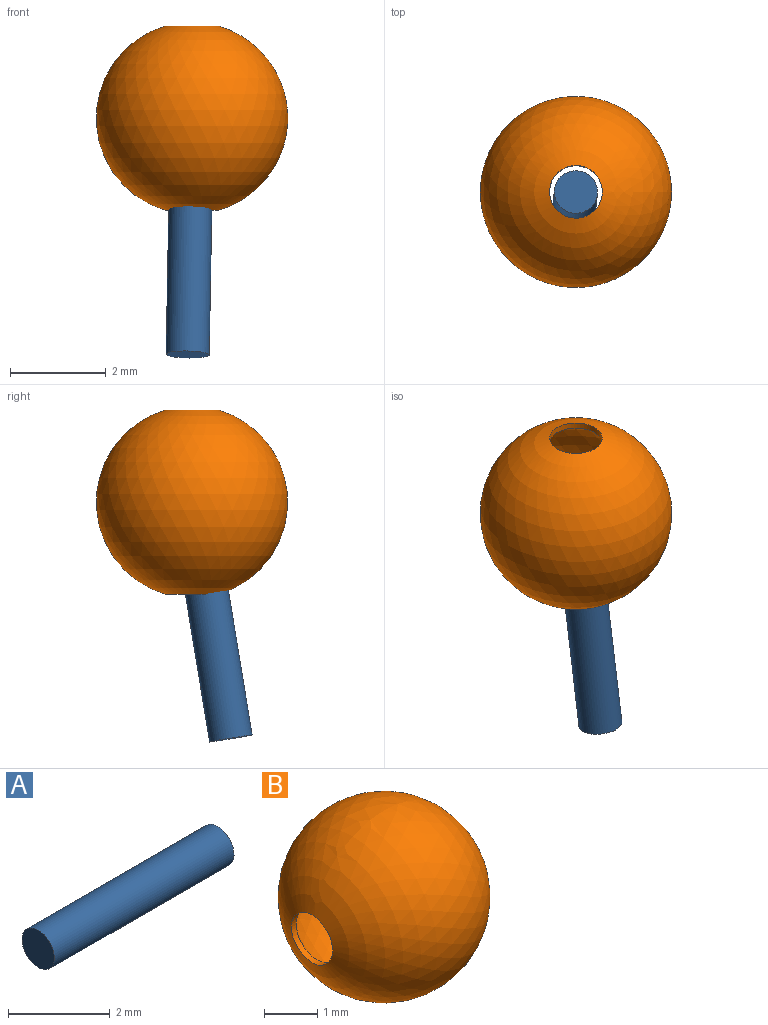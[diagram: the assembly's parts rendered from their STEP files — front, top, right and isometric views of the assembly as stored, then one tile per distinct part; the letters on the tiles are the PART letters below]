
ASSEMBLY  parts=2 mates=1
PART A: 3 faces, bbox 5x0.9x0.9 mm
  f0: plane 0.9x0.9mm, normal (1,0,0), area 0.6mm2, adj f2
  f1: plane 0.9x0.9mm, normal (-1,0,0), area 0.6mm2, adj f2
  f2: cylinder r=0.45mm len=5mm, axis (-1,0,0), area 14.1mm2, adj f0,f1
PART B: 4 faces, bbox 3.8x4x4 mm
  f0: sphere r=2mm, area 48.3mm2, adj f1,f3
  f1: cylinder r=0.55mm len=1.1mm, axis (-1,0,0), area 0.5mm2, adj f0,f2
  f2: sphere r=1.88mm, area 42.2mm2, adj f1,f3
  f3: cylinder r=0.55mm len=1.1mm, axis (-1,0,0), area 0.5mm2, adj f0,f2
PLACE A rot(axis=(-0.03,0.99,-0.14),91.1deg) t=(0,0,0)mm
PLACE B rot(axis=(0,1,0),90deg) t=(0,0,0)mm
MATE ball B.f1 <-> A.f2  axis (0,0,1) through (0,0,0)mm
